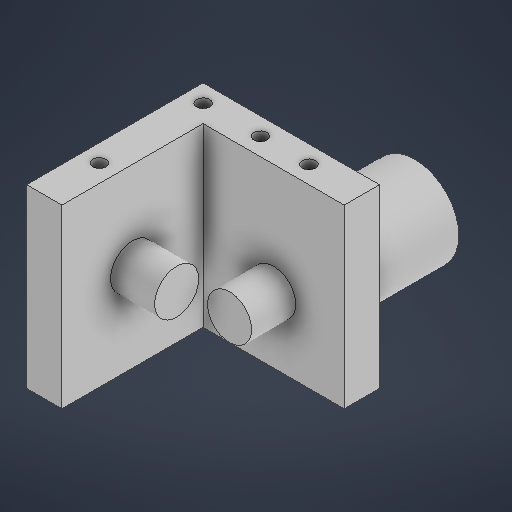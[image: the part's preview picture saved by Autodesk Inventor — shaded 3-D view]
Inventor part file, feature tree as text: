
AUTODESK INVENTOR PART (.ipt)
format: ipt  version: 2025 (Build 290162000, 162)  size: 243,712 bytes
history: native  units: in
note: dims shown in document units (in); Inventor stores cm internally (conversion verified against a paired STEP export)
features: sketch x5, extrude x4, hole x1
ambient origin geometry x8: Origin, YZ Plane, XZ Plane, XY Plane, X Axis, Y Axis, Z Axis, Center Point
bodies: Solid1 (feature_tree)
feature tree (10):
  extrude  "Extrusion1"  Depth=0.315in
  hole  "Hole1"  [1 undecoded]
  extrude  "Extrusion2"  Depth=0.1969in
  extrude  "Extrusion3"  Depth=0.1969in
  extrude  "Extrusion4"  Depth=0.9449in
  sketch  "Sketch1"  dims[d0=1.5748in d1=0.315in]
  sketch  "Sketch2"  dims[d2=0.315in d3=1.5748in]
  sketch  "Sketch3"  dims[d4=1.5748in d5=0.0in d6=0.1969in]
  sketch  "Sketch4"  dims[d7=0.1969in d8=0.1969in]
  sketch  "Sketch5"  dims[d9=0.1969in d10=0.4724in d11=0.4331in d14=0.1181in d15=0.2362in d16=0.1575in d17=0.0787in d18=90.0deg d19=0.4331in d20=0.8108in d21=0.4921in d22=0.9055in d23=0.3937in d24=0.3937in d25=0.0in d26=0.3937in d27=0.5906in d28=0.6299in d29=0.3937in d30=0.0in d31=0.6299in d32=0.7874in d33=0.9449in d34=0.0in]
note: 1 required parameter value undecoded (feature->parameter linkage not recoverable at this tier; creation-order binding heuristic only, values carry confidence <= 0.55)
